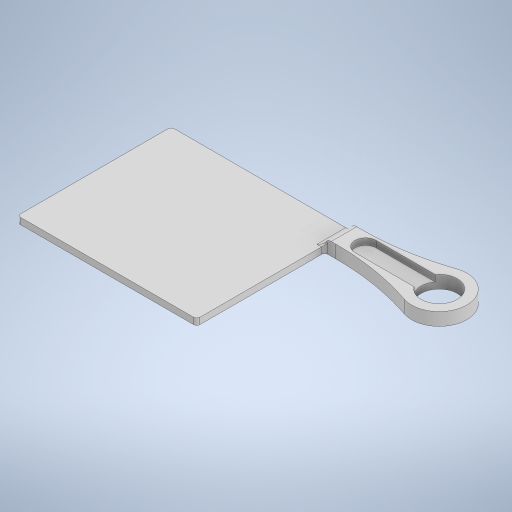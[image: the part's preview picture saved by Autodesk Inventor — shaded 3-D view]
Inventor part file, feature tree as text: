
AUTODESK INVENTOR PART (.ipt)
format: ipt  version: 2023 (Build 270158000, 158)  size: 292,864 bytes
history: native  units: mm
features: extrude x4, sketch x4, fillet x3, projected_geometry x2, other x1
ambient origin geometry x8: Origin, YZ Plane, XZ Plane, XY Plane, X Axis, Y Axis, Z Axis, Center Point
bodies: Body1 (feature_tree)
feature tree (14):
  other  "Bryła1"
  extrude  "Wyciągnięcie proste1"  Depth=5.63mm
  extrude  "Wyciągnięcie proste2"  Depth=1.5mm
  extrude  "Wyciągnięcie proste3"  Depth=43.875mm
  fillet  "Zaokrąglenie1"  Radius=4.0mm
  extrude  "Wyciągnięcie proste4"  Depth=2.0mm TaperAngle=0.0deg
  fillet  "Zaokrąglenie2"  Radius=28.0mm
  fillet  "Zaokrąglenie3"  Radius=20.0mm
  sketch  "Szkic1"
  sketch  "Szkic2"
  projected_geometry  "Pętla rzutowana1"
  sketch  "Szkic3"
  sketch  "Szkic4"
  projected_geometry  "Pętla rzutowana2"
